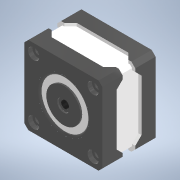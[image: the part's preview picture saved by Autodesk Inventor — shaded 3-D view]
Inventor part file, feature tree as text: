
AUTODESK INVENTOR PART (.ipt)
format: ipt  version: 2021 (Build 250183000, 183)  size: 494,592 bytes
history: native  units: mm
features: sketch x15, extrude x12, projected_geometry x12, fillet x4, mirror x4, reference x4, hole x3, other x2
ambient origin geometry x8: Origin, YZ Plane, XZ Plane, XY Plane, X Axis, Y Axis, Z Axis, Center Point
bodies: Solid1 (feature_tree)
feature tree (56):
  extrude  "Extrusion1"  Depth=2.5mm
  hole  "Hole1"  [1 undecoded]
  extrude  "Extrusion2"  Depth=2.5mm
  fillet  "Fillet1"  Radius=2.5mm
  extrude  "Extrusion3"  Depth=2.5mm
  fillet  "Fillet2"  Radius=34.0mm
  extrude  "Extrusion6"  Depth=31.0mm
  extrude  "Extrusion7"  Depth=15.5mm
  extrude  "Extrusion8"  Depth=2.0mm
  mirror  "Mirror1"
  extrude  "Extrusion9"  Depth=2.0mm
  mirror  "Mirror2"
  mirror  "Mirror3"
  mirror  "Mirror4"
  extrude  "Extrusion12"  Depth=8.0mm
  extrude  "Extrusion11"  Depth=4.0mm
  extrude  "Extrusion10"  Depth=8.0mm
  hole  "Hole5"  [1 undecoded]
  hole  "Hole4"  [1 undecoded]
  extrude  "Extrusion14"  Depth=2.0mm TaperAngle=0.0deg
  fillet  "Fillet4"  Radius=8.0mm
  fillet  "Fillet5"  Radius=4.0mm
  extrude  "Extrusion15"  Depth=2.0mm
  sketch  "Sketch1"  dims[d0=50.0mm d1=2.5mm]
  sketch  "Sketch2"  dims[d2=2.5mm d3=2.5mm]
  projected_geometry  "Projected Loop1"
  sketch  "Sketch3"  dims[d4=2.5mm d5=2.5mm d6=2.5mm]
  sketch  "Sketch4"  dims[d7=2.5mm d8=2.5mm d9=34.0mm d10=0.0mm]
  projected_geometry  "Projected Loop2"
  sketch  "Sketch7"  dims[d11=31.0mm d12=31.0mm]
  projected_geometry  "Projected Loop4"
  sketch  "Sketch8"  dims[d13=15.5mm d14=15.5mm]
  projected_geometry  "Projected Loop5"
  projected_geometry  "Projected Loop6"
  projected_geometry  "Projected Loop7"
  sketch  "Sketch9"  dims[d15=3.458734mm d16=8.0mm d17=4.5mm d18=2.0mm d19=90.0deg d20=10.8mm d21=20.594885mm d22=30.0mm]
  projected_geometry  "Projected Loop8"
  projected_geometry  "Projected Loop9"
  projected_geometry  "Projected Loop10"
  sketch  "Sketch10"  dims[d23=1.0mm d24=0.0mm d25=2.0mm]
  projected_geometry  "Projected Loop11"
  sketch  "Sketch11"  dims[d26=22.0mm d27=8.0mm]
  sketch  "Sketch13"  dims[d28=4.0mm d29=0.0mm d33=0.25mm]
  sketch  "Sketch17"  dims[d37=17.0mm d38=8.0mm]
  sketch  "Sketch18"  dims[d39=4.0mm d40=2.0mm]
  reference  "Reference3"
  reference  "Reference4"
  reference  "Reference5"
  reference  "Reference6"
  sketch  "Sketch20"  dims[d41=2.0mm d42=2.0mm d43=0.0mm]
  sketch  "Sketch21"  dims[d44=2.0mm d45=0.0mm d46=2.0mm d47=0.0mm d48=8.0mm d49=4.0mm]
  projected_geometry  "Projected Loop13"
  projected_geometry  "Projected Loop14"
  sketch  "Sketch22"  dims[d50=4.0mm d51=2.0mm d52=2.0mm d53=0.0mm d55=15.0mm d56=0.0mm d72=6.0mm d73=0.0mm d75=5.0mm d83=5.0mm d84=5.0mm d85=5.0mm d86=5.0mm d87=10.0mm d88=0.0mm d89=4.0mm d90=8.0mm d91=7.25mm d92=2.8mm d93=90.0deg d94=8.0mm d95=20.594885mm d99=4.0mm d111=12.7mm d112=12.7mm d114=50.0mm d115=25.0mm d116=15.0mm d117=7.5mm d118=4.0mm d119=6.0mm d120=7.25mm d121=2.8mm d122=90.0deg d123=8.0mm d124=20.594885mm d125=0.0mm d126=0.0mm d130=2.0mm d131=1.0mm d132=100.0mm d133=0.0mm]
  other  "Mounting Platform.iam"
  other  "Mounting plate:1"
note: 3 required parameter values undecoded (feature->parameter linkage not recoverable at this tier; creation-order binding heuristic only, values carry confidence <= 0.55)
